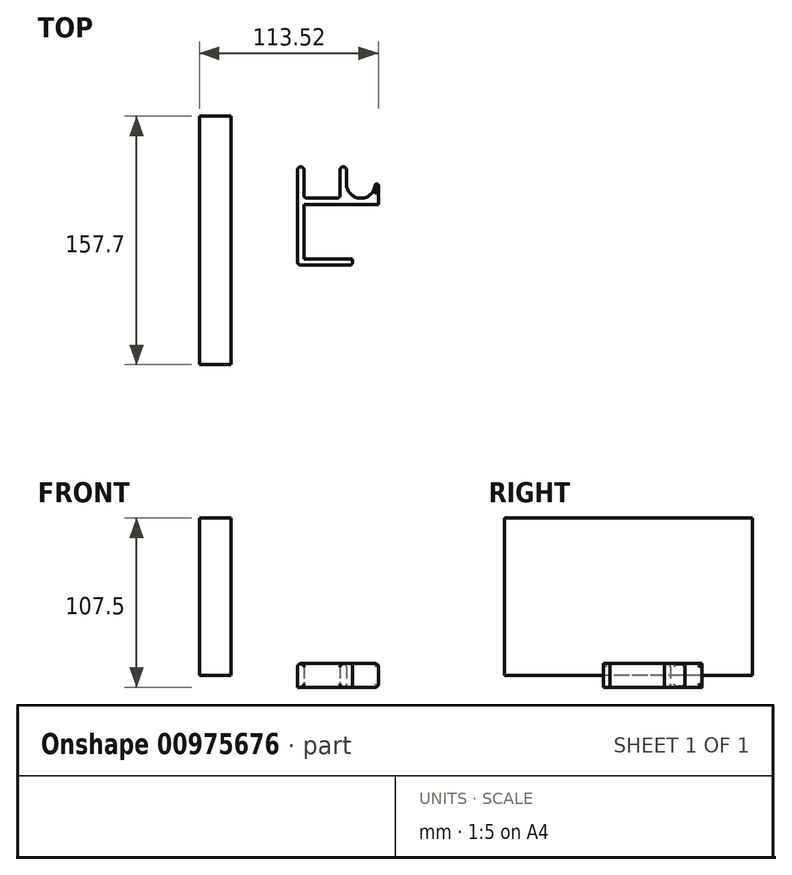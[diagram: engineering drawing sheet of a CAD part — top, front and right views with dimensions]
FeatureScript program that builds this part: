
annotation { "Feature Type Name" : "Feature", "Feature Type Description" : "" }
export const myFeature = defineFeature(function(context is Context, id is Id, definition is map)
    precondition{}
    {
        {
            var Q0;
            Q0=qCreatedBy(makeId("Top.planeOp"),FACE);
            var sketch = newSketch(context, id + "F0", { "sketchPlane" : qUnion([Q0])});
            skLineSegment(sketch, "E0", {"start": v(29.47, 10.54) * mm, "end": v(-1.53, 10.54) * mm});
            skLineSegment(sketch, "E1", {"start": v(-1.53, 10.54) * mm, "end": v(-1.53, -23.96) * mm});
            skLineSegment(sketch, "E2", {"start": v(-1.53, -23.96) * mm, "end": v(29.47, -23.96) * mm});
            skLineSegment(sketch, "E3", {"start": v(29.47, -23.96) * mm, "end": v(29.47, -27.96) * mm});
            skLineSegment(sketch, "E4", {"start": v(29.47, -27.96) * mm, "end": v(-5.53, -27.96) * mm});
            skLineSegment(sketch, "E5", {"start": v(-5.53, -27.96) * mm, "end": v(-5.53, 14.54) * mm});
            skLineSegment(sketch, "E6", {"start": v(-5.53, 14.54) * mm, "end": v(25.47, 14.54) * mm});
            skLineSegment(sketch, "E7.bottom", {"start": v(29.47, -23.96) * mm, "end": v(27.47, -23.96) * mm});
            skLineSegment(sketch, "E8.bottom", {"start": v(29.47, 10.54) * mm, "end": v(27.47, 10.54) * mm});
            skPoint(sketch, "E9", {"position": v(-5.53, -6.71) * mm});
            skLineSegment(sketch, "E10", {"start": v(25.47, 14.54) * mm, "end": v(25.47, 34.54) * mm});
            skLineSegment(sketch, "E11", {"start": v(21.47, 34.54) * mm, "end": v(21.47, 14.54) * mm});
            skLineSegment(sketch, "E12", {"start": v(-5.53, 14.54) * mm, "end": v(-5.53, 34.54) * mm});
            skLineSegment(sketch, "E13", {"start": v(-1.53, 34.54) * mm, "end": v(-1.53, 14.54) * mm});
            skLineSegment(sketch, "E14.bottom", {"start": v(-47.75, 66.63) * mm, "end": v(-67.75, 66.63) * mm});
            skLineSegment(sketch, "E14.top", {"start": v(-47.75, -91.07) * mm, "end": v(-67.75, -91.07) * mm});
            skLineSegment(sketch, "E14.left", {"start": v(-47.75, 66.63) * mm, "end": v(-47.75, -91.07) * mm});
            skLineSegment(sketch, "E14.right", {"start": v(-67.75, 66.63) * mm, "end": v(-67.75, -91.07) * mm});
            skLineSegment(sketch, "E15", {"start": v(-1.53, 34.54) * mm, "end": v(-5.53, 34.54) * mm});
            skLineSegment(sketch, "E16", {"start": v(21.47, 34.54) * mm, "end": v(25.47, 34.54) * mm});
            skArc(sketch, "E17", {"start": v(25.47, 23.69) * mm, "mid": v(34.62, 14.54) * mm, "end": v(43.77, 23.69) * mm});
            skLineSegment(sketch, "E18", {"start": v(45.77, 10.54) * mm, "end": v(29.47, 10.54) * mm});
            skLineSegment(sketch, "E19", {"start": v(34.62, 43.74) * mm, "end": v(34.62, 1.9) * mm, "construction": true});
            skLineSegment(sketch, "E20", {"start": v(43.77, 23.69) * mm, "end": v(45.77, 23.69) * mm});
            skLineSegment(sketch, "E21", {"start": v(45.77, 23.69) * mm, "end": v(45.77, 10.54) * mm});
            skPoint(sketch, "E22.MirrorCS.start.orphan", {"position": v(43.77, 14.54) * mm});
            skPoint(sketch, "E23.orphan", {"position": v(29.47, 14.54) * mm});
            skSolve(sketch);
        }
        {
            var Q0;
            Q0=makeQuery(id+"F0.imprint","IMPRINT",FACE,{"disambiguationData":[TD([[makeQuery(id+"F0.imprint","IMPRINT",EDGE,{"derivedFrom":sQuery(id+"F0.wireOp",EDGE,"E0")}),-1.0]])]});
            var Q1;
            {var subQ0=sQuery(id+"F0.wireOp",EDGE,"E11");Q1=makeQuery(id+"F0.imprint","IMPRINT",FACE,{"disambiguationData":[TD([[makeQuery(id+"F0.imprint","IMPRINT",EDGE,{"derivedFrom":subQ0}),1.0]])]});}
            var Q2;
            {var subQ0=sQuery(id+"F0.wireOp",EDGE,"E12");Q2=makeQuery(id+"F0.imprint","IMPRINT",FACE,{"disambiguationData":[TD([[makeQuery(id+"F0.imprint","IMPRINT",EDGE,{"derivedFrom":subQ0}),-1.0]])]});}
            var Q3;
            {var subQ0=sQuery(id+"F0.wireOp",EDGE,"ZyEKwgAa-MBou-fVqN-9k2C-ZIhGg5rztyWi");var subQ1=sQuery(id+"F0.wireOp",EDGE,"E6");var subQ2=makeQuery(id+"F0.imprint","INTERSECT",VERTEX,{"derivedFrom":[subQ1,subQ0]});Q3=makeQuery(id+"F0.imprint","IMPRINT",FACE,{"disambiguationData":[TD([[makeQuery(id+"F0.imprint","IMPRINT",EDGE,{"disambiguationData":[TD([[subQ2,1.0]])],"derivedFrom":subQ1}),1.0]])]});}
            var Q4;
            {var subQ0=sQuery(id+"F0.wireOp",EDGE,"E22.MirrorCS");Q4=makeQuery(id+"F0.imprint","IMPRINT",FACE,{"disambiguationData":[TD([[makeQuery(id+"F0.imprint","IMPRINT",EDGE,{"derivedFrom":subQ0}),1.0]])]});}
            var Q5;
            {var subQ2=sQuery(id+"F0.wireOp",EDGE,"E22.MirrorCS");Q5=makeQuery(id+"F0.imprint","IMPRINT",FACE,{"disambiguationData":[TD([[makeQuery(id+"F0.imprint","IMPRINT",EDGE,{"derivedFrom":subQ2}),-1.0]])]});}
            extrude(context, id + "F1", {"entities" : qUnion([Q0, Q1, Q2, Q3, Q4, Q5]), "endBound" : BoundingType.SYMMETRIC, "depth" : 15 * mm, "offsetDistance" : 25 * mm});
        }
        {
            var Q0;
            {var subQ0=sQuery(id+"F0.wireOp",EDGE,"E6");Q0=makeQuery(id+"F1.opExtrude","CAP_EDGE",EDGE,{"disambiguationData":[OSD([subQ0]),TDD([makeQuery(id+"F0.imprint","IMPRINT",EDGE,{"disambiguationData":[TD([[makeQuery(id+"F0.imprint","INTERSECT",VERTEX,{"derivedFrom":[subQ0,sQuery(id+"F0.wireOp",EDGE,"E11")]}),1.0]])],"derivedFrom":subQ0})])],"isStart":false});}
            var Q1;
            {var subQ0=sQuery(id+"F0.wireOp",EDGE,"E6");Q1=makeQuery(id+"F1.opExtrude","CAP_EDGE",EDGE,{"disambiguationData":[OSD([subQ0]),TDD([makeQuery(id+"F0.imprint","IMPRINT",EDGE,{"disambiguationData":[TD([[makeQuery(id+"F0.imprint","INTERSECT",VERTEX,{"derivedFrom":[sQuery(id+"F0.wireOp",EDGE,"8vs2pwZv-PnCw-5P7d-vrQF-311Tecl8wrVt"),subQ0]}),1.0]])],"derivedFrom":subQ0})])],"isStart":false});}
            var Q2;
            {var subQ0=sQuery(id+"F0.wireOp",EDGE,"E6");Q2=makeQuery(id+"F1.opExtrude","CAP_EDGE",EDGE,{"disambiguationData":[OSD([subQ0]),TDD([makeQuery(id+"F0.imprint","IMPRINT",EDGE,{"disambiguationData":[TD([[makeQuery(id+"F0.imprint","INTERSECT",VERTEX,{"derivedFrom":[subQ0,sQuery(id+"F0.wireOp",EDGE,"E11")]}),1.0]])],"derivedFrom":subQ0})])],"isStart":true});}
            var Q3;
            {var subQ0=sQuery(id+"F0.wireOp",EDGE,"E6");Q3=makeQuery(id+"F1.opExtrude","CAP_EDGE",EDGE,{"disambiguationData":[OSD([subQ0]),TDD([makeQuery(id+"F0.imprint","IMPRINT",EDGE,{"disambiguationData":[TD([[makeQuery(id+"F0.imprint","INTERSECT",VERTEX,{"derivedFrom":[sQuery(id+"F0.wireOp",EDGE,"8vs2pwZv-PnCw-5P7d-vrQF-311Tecl8wrVt"),subQ0]}),1.0]])],"derivedFrom":subQ0})])],"isStart":true});}
            var Q4;
            Q4=makeQuery(id+"F1.opExtrude","CAP_EDGE",EDGE,{"disambiguationData":[OSD([sQuery(id+"F0.wireOp",EDGE,"E5"),sQuery(id+"F0.wireOp",EDGE,"E12")])],"isStart":false});
            var Q5;
            Q5=makeQuery(id+"F1.opExtrude","SWEPT_EDGE",EDGE,{"disambiguationData":[OSD([sQuery(id+"F0.wireOp",EDGE,"E3"),sQuery(id+"F0.wireOp",EDGE,"E4")])]});
            var Q6;
            Q6=makeQuery(id+"F1.opExtrude","SWEPT_EDGE",EDGE,{"disambiguationData":[OSD([sQuery(id+"F0.wireOp",EDGE,"E4"),sQuery(id+"F0.wireOp",EDGE,"E5")])]});
            var Q7;
            Q7=makeQuery(id+"F1.opExtrude","SWEPT_EDGE",EDGE,{"disambiguationData":[OSD([sQuery(id+"F0.wireOp",EDGE,"8vs2pwZv-PnCw-5P7d-vrQF-311Tecl8wrVt"),sQuery(id+"F0.wireOp",EDGE,"E6")])]});
            var Q8;
            Q8=makeQuery(id+"F1.opExtrude","SWEPT_EDGE",EDGE,{"disambiguationData":[OSD([sQuery(id+"F0.wireOp",EDGE,"E10"),sQuery(id+"F0.wireOp",EDGE,"E16")])]});
            var Q9;
            Q9=makeQuery(id+"F1.opExtrude","SWEPT_EDGE",EDGE,{"disambiguationData":[OSD([sQuery(id+"F0.wireOp",EDGE,"E13"),sQuery(id+"F0.wireOp",EDGE,"E15")])]});
            var Q10;
            Q10=makeQuery(id+"F1.opExtrude","SWEPT_EDGE",EDGE,{"disambiguationData":[OSD([sQuery(id+"F0.wireOp",EDGE,"E11"),sQuery(id+"F0.wireOp",EDGE,"E16")])]});
            var Q11;
            Q11=makeQuery(id+"F1.opExtrude","SWEPT_EDGE",EDGE,{"disambiguationData":[OSD([sQuery(id+"F0.wireOp",EDGE,"E12"),sQuery(id+"F0.wireOp",EDGE,"E15")])]});
            var Q12;
            Q12=makeQuery(id+"F1.opExtrude","SWEPT_EDGE",EDGE,{"disambiguationData":[OSD([sQuery(id+"F0.wireOp",EDGE,"E6"),sQuery(id+"F0.wireOp",EDGE,"E10")])]});
            var Q13;
            Q13=makeQuery(id+"F1.opExtrude","SWEPT_EDGE",EDGE,{"disambiguationData":[OSD([sQuery(id+"F0.wireOp",EDGE,"E6"),sQuery(id+"F0.wireOp",EDGE,"E11")])]});
            var Q14;
            Q14=makeQuery(id+"F1.opExtrude","SWEPT_EDGE",EDGE,{"disambiguationData":[OSD([sQuery(id+"F0.wireOp",EDGE,"E6"),sQuery(id+"F0.wireOp",EDGE,"E13")])]});
            var Q15;
            Q15=makeQuery(id+"F1.opExtrude","CAP_EDGE",EDGE,{"disambiguationData":[OSD([sQuery(id+"F0.wireOp",EDGE,"E21")])],"isStart":false});
            var Q16;
            Q16=makeQuery(id+"F1.opExtrude","CAP_EDGE",EDGE,{"disambiguationData":[OSD([sQuery(id+"F0.wireOp",EDGE,"E21")])],"isStart":true});
            var Q17;
            Q17=makeQuery(id+"F1.opExtrude","CAP_EDGE",EDGE,{"disambiguationData":[OSD([sQuery(id+"F0.wireOp",EDGE,"E17")])],"isStart":false});
            var Q18;
            Q18=makeQuery(id+"F1.opExtrude","CAP_EDGE",EDGE,{"disambiguationData":[OSD([sQuery(id+"F0.wireOp",EDGE,"E17")])],"isStart":true});
            var Q19;
            Q19=makeQuery(id+"F1.opExtrude","CAP_EDGE",EDGE,{"disambiguationData":[OSD([sQuery(id+"F0.wireOp",EDGE,"E10")])],"isStart":false});
            var Q20;
            Q20=makeQuery(id+"F1.opExtrude","CAP_EDGE",EDGE,{"disambiguationData":[OSD([sQuery(id+"F0.wireOp",EDGE,"E10")])],"isStart":true});
            fillet(context, id + "F2", {"entities" : qUnion([Q0, Q1, Q2, Q3, Q4, Q5, Q6, Q7, Q8, Q9, Q10, Q11, Q12, Q13, Q14, Q15, Q16, Q17, Q18, Q19, Q20]), "radius" : 2 * mm, "tangentPropagation" : true, "defaultsChanged" : false, "vertexSettings" : [], "allowEdgeOverflow" : false});
        }
        {
            var Q0;
            Q0=makeQuery(id+"F0.imprint","IMPRINT",FACE,{"disambiguationData":[TD([[makeQuery(id+"F0.imprint","IMPRINT",EDGE,{"derivedFrom":sQuery(id+"F0.wireOp",EDGE,"E14.bottom")}),1.0]])]});
            extrude(context, id + "F3", {"entities" : qUnion([Q0]), "depth" : 100 * mm, "offsetDistance" : 25 * mm});
        }
        {
            var Q0;
            Q0=makeQuery(id+"F1.opExtrude","SWEPT_EDGE",EDGE,{"disambiguationData":[OSD([sQuery(id+"F0.wireOp",EDGE,"E17"),sQuery(id+"F0.wireOp",EDGE,"E20")])]});
            var Q1;
            Q1=makeQuery(id+"F1.opExtrude","SWEPT_EDGE",EDGE,{"disambiguationData":[OSD([sQuery(id+"F0.wireOp",EDGE,"E20"),sQuery(id+"F0.wireOp",EDGE,"E21")])]});
            fillet(context, id + "F4", {"entities" : qUnion([Q0, Q1]), "tangentPropagation" : true, "radius" : 1 * mm, "defaultsChanged" : true, "vertexSettings" : [], "allowEdgeOverflow" : false});
        }
    });
